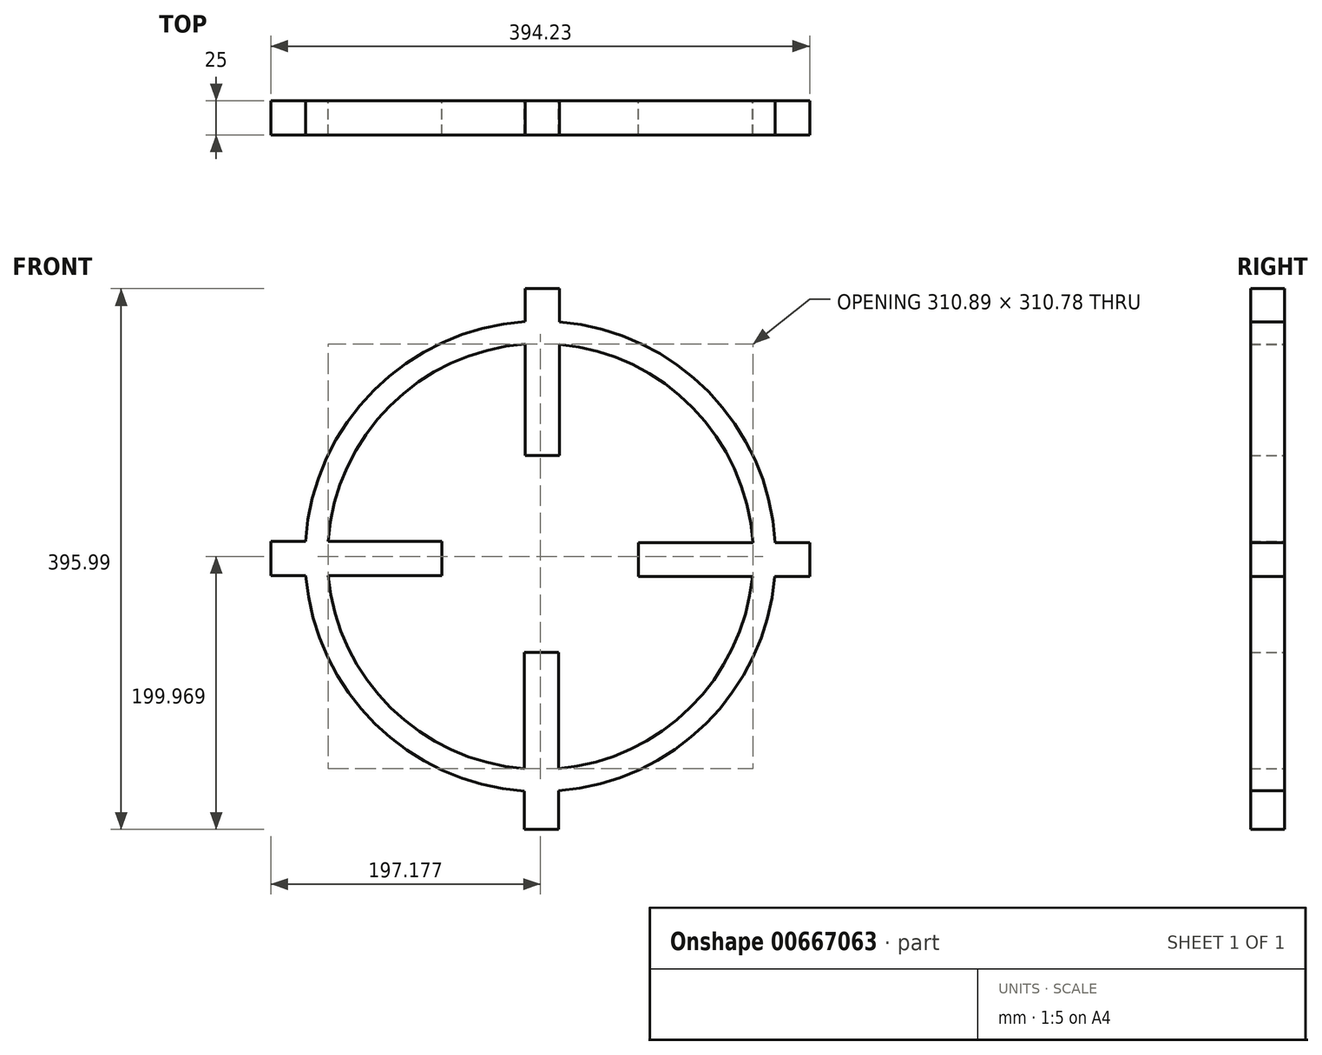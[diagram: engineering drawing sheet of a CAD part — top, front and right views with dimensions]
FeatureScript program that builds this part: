
annotation { "Feature Type Name" : "Feature", "Feature Type Description" : "" }
export const myFeature = defineFeature(function(context is Context, id is Id, definition is map)
    precondition{}
    {
        {
            var Q0;
            Q0=qCreatedBy(makeId("Front.planeOp"),FACE);
            var sketch = newSketch(context, id + "F0", { "sketchPlane" : qUnion([Q0])});
            skCircle(sketch, "E0", {"center": v(0, 0) * mm, "radius": 172.2 * mm});
            skCircle(sketch, "E1", {"center": v(0, 0) * mm, "radius": 155.8 * mm});
            skLineSegment(sketch, "E2.bottom", {"start": v(-172.2, -14) * mm, "end": v(-171.62, -14) * mm});
            skLineSegment(sketch, "E2.top", {"start": v(-172.2, 11) * mm, "end": v(-171.84, 11) * mm});
            skLineSegment(sketch, "E2.left", {"start": v(-172.2, -14) * mm, "end": v(-172.2, 11) * mm});
            skLineSegment(sketch, "E2.right", {"start": v(-72.2, -14) * mm, "end": v(-72.2, 11) * mm});
            skLineSegment(sketch, "E3.bottom", {"start": v(155.47, 10.2) * mm, "end": v(71.88, 10.2) * mm});
            skLineSegment(sketch, "E3.top", {"start": v(171.88, -14.8) * mm, "end": v(171.55, -14.8) * mm});
            skLineSegment(sketch, "E3.left", {"start": v(171.88, 10.2) * mm, "end": v(171.88, -14.8) * mm});
            skLineSegment(sketch, "E3.right", {"start": v(71.88, 10.2) * mm, "end": v(71.88, -14.8) * mm});
            skLineSegment(sketch, "E4.right", {"start": v(-11, 73.87) * mm, "end": v(14, 73.87) * mm});
            skLineSegment(sketch, "E5.bottom", {"start": v(13.2, -155.25) * mm, "end": v(13.2, -70.2) * mm});
            skLineSegment(sketch, "E5.top", {"start": v(-11.8, -155.36) * mm, "end": v(-11.8, -70.2) * mm});
            skLineSegment(sketch, "E5.right", {"start": v(13.2, -70.2) * mm, "end": v(-11.8, -70.2) * mm});
            skLineSegment(sketch, "E6.trimOffspring", {"start": v(155.1, -14.8) * mm, "end": v(71.88, -14.8) * mm});
            skLineSegment(sketch, "E7.trimOffspring", {"start": v(14, 155.18) * mm, "end": v(14, 73.87) * mm});
            skLineSegment(sketch, "E8.trimOffspring", {"start": v(-11, 155.42) * mm, "end": v(-11, 73.87) * mm});
            skLineSegment(sketch, "E9.trimOffspring", {"start": v(-155.18, -14) * mm, "end": v(-72.2, -14) * mm});
            skLineSegment(sketch, "E10.trimOffspring", {"start": v(-155.42, 11) * mm, "end": v(-72.2, 11) * mm});
            skLineSegment(sketch, "E11", {"start": v(-171.84, 11) * mm, "end": v(-197.15, 11) * mm});
            skLineSegment(sketch, "E12", {"start": v(-171.62, -14) * mm, "end": v(-197.15, -14) * mm});
            skLineSegment(sketch, "E13", {"start": v(-197.15, -14) * mm, "end": v(-197.15, 11) * mm});
            skLineSegment(sketch, "E14", {"start": v(171.88, 10.2) * mm, "end": v(197.08, 10.2) * mm});
            skLineSegment(sketch, "E15", {"start": v(197.08, -14.8) * mm, "end": v(197.08, 10.2) * mm});
            skLineSegment(sketch, "E16", {"start": v(197.08, -14.8) * mm, "end": v(171.88, -14.8) * mm});
            skLineSegment(sketch, "E17", {"start": v(-11, 155.42) * mm, "end": v(-11, 196.05) * mm});
            skLineSegment(sketch, "E18", {"start": v(14, 196.05) * mm, "end": v(-11, 196.05) * mm});
            skLineSegment(sketch, "E19", {"start": v(14, 196.05) * mm, "end": v(14, 155.18) * mm});
            skLineSegment(sketch, "E20", {"start": v(-11.8, -155.36) * mm, "end": v(-11.8, -199.94) * mm});
            skLineSegment(sketch, "E21", {"start": v(13.2, -155.25) * mm, "end": v(13.2, -199.94) * mm});
            skLineSegment(sketch, "E22", {"start": v(13.2, -199.94) * mm, "end": v(-11.8, -199.94) * mm});
            skSolve(sketch);
        }
        {
            var Q0;
            Q0 = qSketchRegion(id + "F0", true);
            var Q1;
            Q1=makeQuery(id+"F0.imprint","IMPRINT",FACE,{"disambiguationData":[TD([[makeQuery(id+"F0.imprint","IMPRINT",EDGE,{"derivedFrom":sQuery(id+"F0.wireOp",EDGE,"E2.right")}),1.0]])]});
            var Q2;
            {var subQ0=sQuery(id+"F0.wireOp",EDGE,"E5.bottom");Q2=makeQuery(id+"F0.imprint","IMPRINT",FACE,{"disambiguationData":[TD([[makeQuery(id+"F0.imprint","IMPRINT",EDGE,{"derivedFrom":subQ0}),1.0]])]});}
            var Q3;
            {var subQ0=sQuery(id+"F0.wireOp",EDGE,"E3.bottom");Q3=makeQuery(id+"F0.imprint","IMPRINT",FACE,{"disambiguationData":[TD([[makeQuery(id+"F0.imprint","IMPRINT",EDGE,{"derivedFrom":subQ0}),1.0]])]});}
            var Q4;
            Q4=makeQuery(id+"F0.imprint","IMPRINT",FACE,{"disambiguationData":[TD([[makeQuery(id+"F0.imprint","IMPRINT",EDGE,{"derivedFrom":sQuery(id+"F0.wireOp",EDGE,"E4.right")}),1.0]])]});
            extrude(context, id + "F1", {"entities" : qUnion([Q0, Q1, Q2, Q3, Q4]), "depth" : 25 * mm, "offsetDistance" : 25 * mm});
        }
    });
